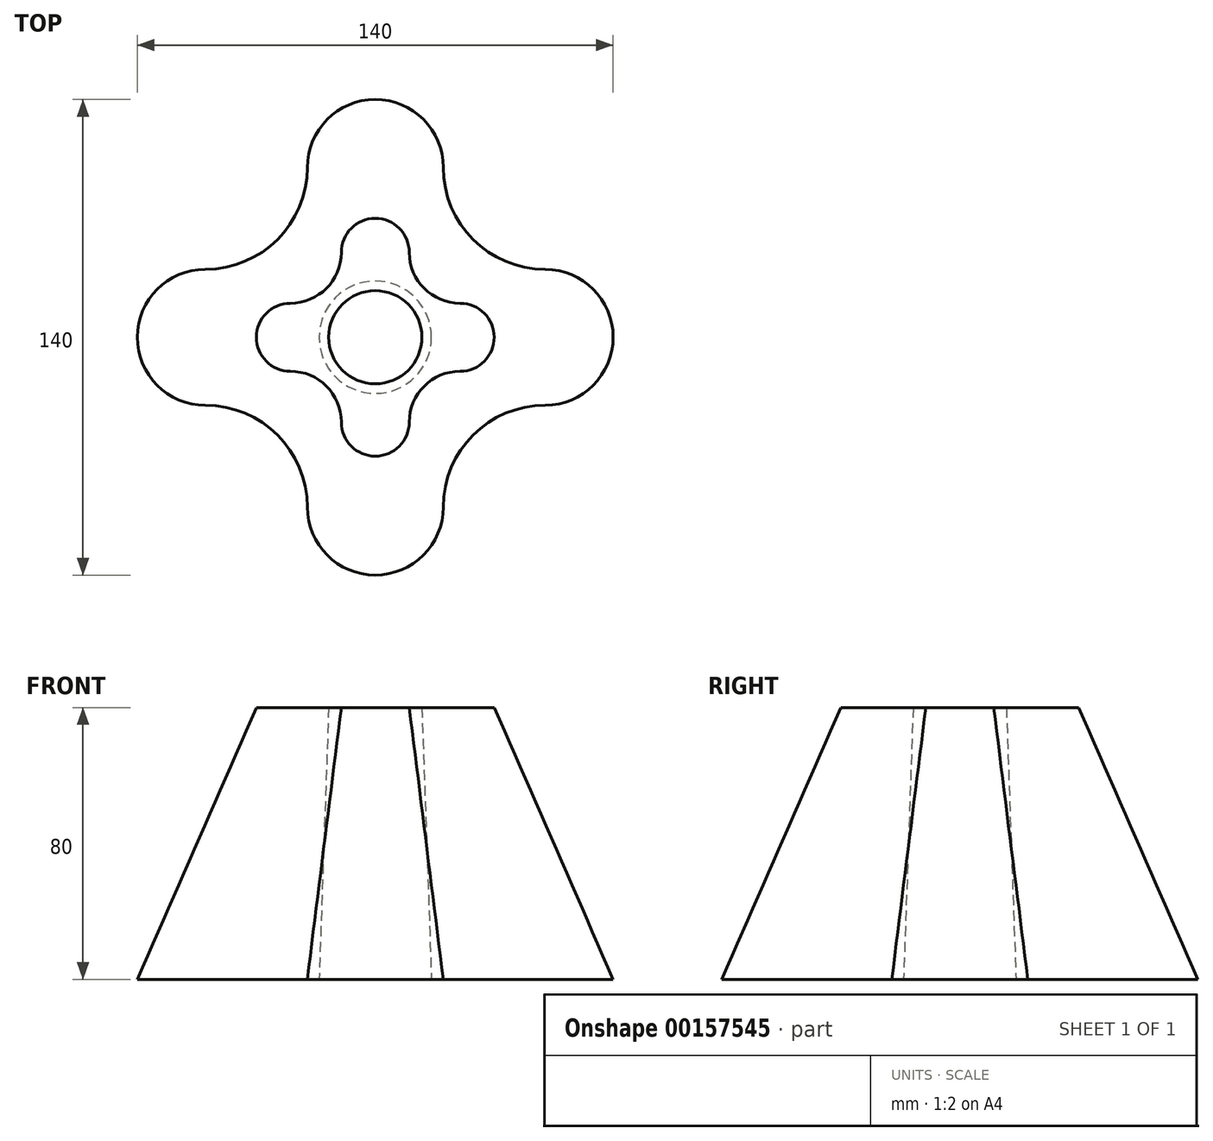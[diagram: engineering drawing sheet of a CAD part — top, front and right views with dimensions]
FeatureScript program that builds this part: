
annotation { "Feature Type Name" : "Feature", "Feature Type Description" : "" }
export const myFeature = defineFeature(function(context is Context, id is Id, definition is map)
    precondition{}
    {
        {
            var Q0;
            Q0=qCreatedBy(makeId("Top.planeOp"),FACE);
            var sketch = newSketch(context, id + "F0", { "sketchPlane" : qUnion([Q0])});
            skLineSegment(sketch, "E0.bottom", {"start": v(50, 50) * mm, "end": v(-50, 50) * mm, "construction": true});
            skLineSegment(sketch, "E0.top", {"start": v(50, -50) * mm, "end": v(-50, -50) * mm, "construction": true});
            skLineSegment(sketch, "E0.left", {"start": v(50, 50) * mm, "end": v(50, -50) * mm, "construction": true});
            skLineSegment(sketch, "E0.right", {"start": v(-50, 50) * mm, "end": v(-50, -50) * mm, "construction": true});
            skPoint(sketch, "E0.middle", {"position": v(0, 0) * mm});
            skArc(sketch, "E1", {"start": v(20, 50) * mm, "mid": v(0, 70) * mm, "end": v(-20, 50) * mm});
            skArc(sketch, "E2", {"start": v(-20, -50) * mm, "mid": v(0, -70) * mm, "end": v(20, -50) * mm});
            skArc(sketch, "E3", {"start": v(-50, 20) * mm, "mid": v(-70, 0) * mm, "end": v(-50, -20) * mm});
            skArc(sketch, "E4", {"start": v(50, 20) * mm, "mid": v(70, 0) * mm, "end": v(50, -20) * mm});
            skArc(sketch, "E5", {"start": v(-50, 20) * mm, "mid": v(-28.79, 28.79) * mm, "end": v(-20, 50) * mm});
            skArc(sketch, "E6", {"start": v(20, 50) * mm, "mid": v(28.79, 28.79) * mm, "end": v(50, 20) * mm});
            skArc(sketch, "E7", {"start": v(50, -20) * mm, "mid": v(28.79, -28.79) * mm, "end": v(20, -50) * mm});
            skArc(sketch, "E8", {"start": v(-20, -50) * mm, "mid": v(-28.79, -28.79) * mm, "end": v(-50, -20) * mm});
            skSolve(sketch);
        }
        {
            var Q0;
            Q0=qCreatedBy(makeId("Front.planeOp"),FACE);
            var sketch = newSketch(context, id + "F1", { "sketchPlane" : qUnion([Q0])});
            skLineSegment(sketch, "E9", {"start": v(0, 0) * mm, "end": v(0, 111.25) * mm, "construction": true});
            skPoint(sketch, "E10", {"position": v(0, 80) * mm});
            skSolve(sketch);
        }
        {
            var Q0;
            Q0=qCreatedBy(makeId("Top.planeOp"),FACE);
            var Q1;
            Q1=sQuery(id+"F1.wireOp",VERTEX,"E10");
            cPlane(context, id + "F2", {"entities" : qUnion([Q0, Q1]), "cplaneType" : CPlaneType.PLANE_POINT, "offset" : 25 * mm, "width" : 150 * mm, "height" : 150 * mm});
        }
        {
            var Q0;
            Q0=qCreatedBy(id+"F2.planeOp",FACE);
            var sketch = newSketch(context, id + "F3", { "sketchPlane" : qUnion([Q0])});
            skLineSegment(sketch, "E11.bottom", {"start": v(25, 25) * mm, "end": v(-25, 25) * mm, "construction": true});
            skLineSegment(sketch, "E11.top", {"start": v(25, -25) * mm, "end": v(-25, -25) * mm, "construction": true});
            skLineSegment(sketch, "E11.left", {"start": v(25, 25) * mm, "end": v(25, -25) * mm, "construction": true});
            skLineSegment(sketch, "E11.right", {"start": v(-25, 25) * mm, "end": v(-25, -25) * mm, "construction": true});
            skPoint(sketch, "E11.middle", {"position": v(0, 0) * mm});
            skArc(sketch, "E12", {"start": v(10, 25) * mm, "mid": v(0, 35) * mm, "end": v(-10, 25) * mm});
            skArc(sketch, "E13", {"start": v(-10, -25) * mm, "mid": v(0, -35) * mm, "end": v(10, -25) * mm});
            skArc(sketch, "E14", {"start": v(-25, 10) * mm, "mid": v(-35, 0) * mm, "end": v(-25, -10) * mm});
            skArc(sketch, "E15", {"start": v(25, 10) * mm, "mid": v(35, 0) * mm, "end": v(25, -10) * mm});
            skArc(sketch, "E16", {"start": v(-25, 10) * mm, "mid": v(-14.4, 14.4) * mm, "end": v(-10, 25) * mm});
            skArc(sketch, "E17", {"start": v(10, 25) * mm, "mid": v(14.4, 14.4) * mm, "end": v(25, 10) * mm});
            skArc(sketch, "E18", {"start": v(25, -10) * mm, "mid": v(14.4, -14.4) * mm, "end": v(10, -25) * mm});
            skArc(sketch, "E19", {"start": v(-10, -25) * mm, "mid": v(-14.4, -14.4) * mm, "end": v(-25, -10) * mm});
            skSolve(sketch);
        }
        {
            var Q0;
            Q0=makeQuery(id+"F0.imprint","IMPRINT",FACE,{"disambiguationData":[TD([[makeQuery(id+"F0.imprint","IMPRINT",EDGE,{"derivedFrom":sQuery(id+"F0.wireOp",EDGE,"E1")}),1.0]])]});
            var Q1;
            Q1=makeQuery(id+"F3.imprint","IMPRINT",FACE,{"disambiguationData":[TD([[makeQuery(id+"F3.imprint","IMPRINT",EDGE,{"derivedFrom":sQuery(id+"F3.wireOp",EDGE,"E12")}),1.0]])]});
            loft(context, id + "F4", {"sheetProfilesArray" : [{ "sheetProfileEntities" : qUnion([Q0]) }, { "sheetProfileEntities" : qUnion([Q1]) }]});
        }
        {
            var Q0;
            Q0=qCreatedBy(makeId("Top.planeOp"),FACE);
            var sketch = newSketch(context, id + "F5", { "sketchPlane" : qUnion([Q0])});
            skCircle(sketch, "E20", {"center": v(0, 0) * mm, "radius": 16.54 * mm});
            skSolve(sketch);
        }
        {
            var Q0;
            Q0=makeQuery(id+"F3.imprint","IMPRINT",FACE,{"disambiguationData":[TD([[makeQuery(id+"F3.imprint","IMPRINT",EDGE,{"derivedFrom":sQuery(id+"F3.wireOp",EDGE,"E12")}),1.0]])]});
            var sketch = newSketch(context, id + "F6", { "sketchPlane" : qUnion([Q0])});
            skCircle(sketch, "E21", {"center": v(0, 0) * mm, "radius": 13.7 * mm});
            skSolve(sketch);
        }
        {
            var Q1;
            Q1=makeQuery(id+"F5.imprint","IMPRINT",FACE,{"disambiguationData":[TD([[makeQuery(id+"F5.imprint","IMPRINT",EDGE,{"derivedFrom":sQuery(id+"F5.wireOp",EDGE,"E20")}),1.0]])]});
            var Q2;
            Q2=makeQuery(id+"F6.imprint","IMPRINT",FACE,{"disambiguationData":[TD([[makeQuery(id+"F6.imprint","IMPRINT",EDGE,{"derivedFrom":sQuery(id+"F6.wireOp",EDGE,"E21")}),1.0]])]});
            loft(context, id + "F7", {"operationType" : NewBodyOperationType.REMOVE, "sheetProfilesArray" : [{ "sheetProfileEntities" : qUnion([Q1]) }, { "sheetProfileEntities" : qUnion([Q2]) }]});
        }
    });
